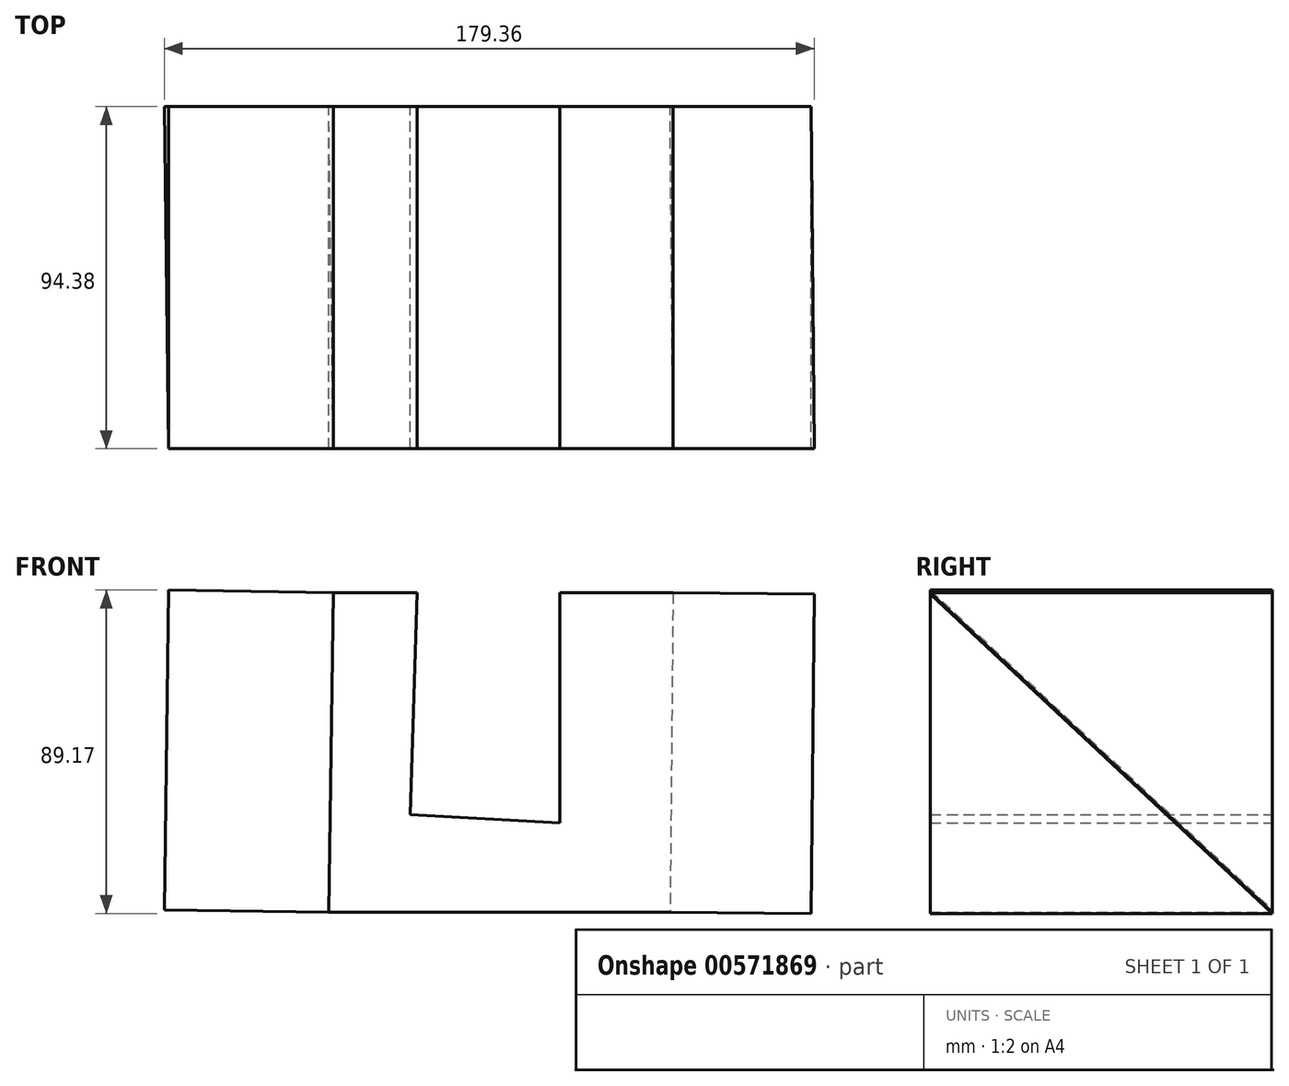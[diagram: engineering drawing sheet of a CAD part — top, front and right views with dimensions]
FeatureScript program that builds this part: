
annotation { "Feature Type Name" : "Feature", "Feature Type Description" : "" }
export const myFeature = defineFeature(function(context is Context, id is Id, definition is map)
    precondition{}
    {
        {
            var Q0;
            Q0=qCreatedBy(makeId("Front.planeOp"),FACE);
            var sketch = newSketch(context, id + "F0", { "sketchPlane" : qUnion([Q0])});
            skLineSegment(sketch, "E0", {"start": v(-44.08, 37.03) * mm, "end": v(-20.98, 37.03) * mm});
            skLineSegment(sketch, "E1", {"start": v(-20.98, 37.03) * mm, "end": v(-22.83, -24.29) * mm});
            skLineSegment(sketch, "E2", {"start": v(-22.83, -24.29) * mm, "end": v(18.44, -26.48) * mm});
            skLineSegment(sketch, "E3", {"start": v(18.44, -26.48) * mm, "end": v(18.44, 36.92) * mm});
            skLineSegment(sketch, "E4", {"start": v(18.44, 36.92) * mm, "end": v(49.7, 36.92) * mm});
            skLineSegment(sketch, "E5", {"start": v(49.7, 36.92) * mm, "end": v(48.87, -51.14) * mm});
            skLineSegment(sketch, "E6", {"start": v(48.87, -51.14) * mm, "end": v(-45.33, -51.14) * mm});
            skLineSegment(sketch, "E7", {"start": v(-45.33, -51.14) * mm, "end": v(-44.08, 37.03) * mm});
            skSolve(sketch);
        }
        {
            var Q0;
            Q0=makeQuery(id+"F0.imprint","IMPRINT",FACE,{"disambiguationData":[TD([[makeQuery(id+"F0.imprint","IMPRINT",EDGE,{"derivedFrom":sQuery(id+"F0.wireOp",EDGE,"E0")}),-1.0]])]});
            extrude(context, id + "F1", {"entities" : qUnion([Q0]), "depth" : 94.38 * mm, "offsetDistance" : 25.4 * mm});
        }
        {
            var Q0;
            Q0=makeQuery(id+"F1.opExtrude","SWEPT_FACE",FACE,{"disambiguationData":[OSD([sQuery(id+"F0.wireOp",EDGE,"E7")])]});
            var sketch = newSketch(context, id + "F2", { "sketchPlane" : qUnion([Q0])});
            skLineSegment(sketch, "E8", {"start": v(94.38, 36.4) * mm, "end": v(0, -51.78) * mm});
            skLineSegment(sketch, "E9", {"start": v(0, -51.78) * mm, "end": v(0, 36.4) * mm});
            skLineSegment(sketch, "E10", {"start": v(0, 36.4) * mm, "end": v(94.38, 36.4) * mm});
            skSolve(sketch);
        }
        {
            var Q0;
            Q0=makeQuery(id+"F2.imprint","IMPRINT",FACE,{"disambiguationData":[TD([[makeQuery(id+"F2.imprint","IMPRINT",EDGE,{"derivedFrom":sQuery(id+"F2.wireOp",EDGE,"E8")}),-1.0]])]});
            extrude(context, id + "F3", {"entities" : qUnion([Q0]), "operationType" : NewBodyOperationType.ADD, "depth" : 45.38 * mm, "offsetDistance" : 25.4 * mm});
        }
        {
            var Q0;
            Q0=makeQuery(id+"F1.opExtrude","SWEPT_FACE",FACE,{"disambiguationData":[OSD([sQuery(id+"F0.wireOp",EDGE,"E5")])]});
            var sketch = newSketch(context, id + "F4", { "sketchPlane" : qUnion([Q0])});
            skLineSegment(sketch, "E11", {"start": v(-94.38, 37.38) * mm, "end": v(0, -50.69) * mm});
            skLineSegment(sketch, "E12", {"start": v(0, -50.69) * mm, "end": v(-94.38, -50.69) * mm});
            skLineSegment(sketch, "E13", {"start": v(-94.38, -50.69) * mm, "end": v(-94.38, 37.9) * mm});
            skSolve(sketch);
        }
        {
            var Q0;
            {var subQ0=sQuery(id+"F4.wireOp",EDGE,"E11");Q0=makeQuery(id+"F4.imprint","IMPRINT",FACE,{"disambiguationData":[TD([[makeQuery(id+"F4.imprint","IMPRINT",EDGE,{"derivedFrom":subQ0}),-1.0]])]});}
            extrude(context, id + "F5", {"entities" : qUnion([Q0]), "operationType" : NewBodyOperationType.ADD, "depth" : 38.96 * mm, "offsetDistance" : 25.4 * mm});
        }
    });
